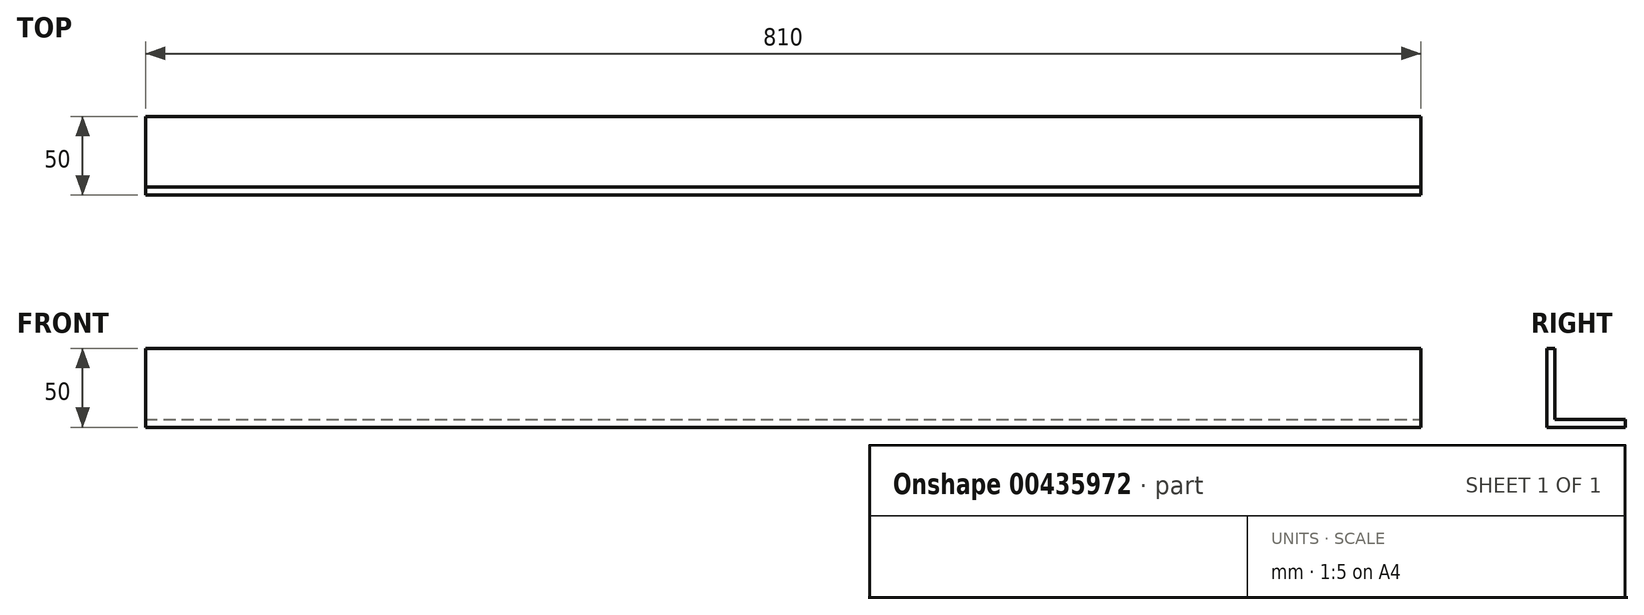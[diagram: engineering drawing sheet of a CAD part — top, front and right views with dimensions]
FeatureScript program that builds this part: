
annotation { "Feature Type Name" : "Feature", "Feature Type Description" : "" }
export const myFeature = defineFeature(function(context is Context, id is Id, definition is map)
    precondition{}
    {
        {
            var Q0;
            Q0=qCreatedBy(makeId("Right.planeOp"),FACE);
            var sketch = newSketch(context, id + "F0", { "sketchPlane" : qUnion([Q0])});
            skLineSegment(sketch, "E0.bottom", {"start": v(0, 0) * mm, "end": v(-50, 0) * mm});
            skLineSegment(sketch, "E0.right", {"start": v(-50, 0) * mm, "end": v(-50, 50) * mm});
            skLineSegment(sketch, "E1.0", {"start": v(0, 5) * mm, "end": v(-45, 5) * mm});
            skLineSegment(sketch, "E2.0", {"start": v(-45, 5) * mm, "end": v(-45, 50) * mm});
            skLineSegment(sketch, "E3", {"start": v(-50, 50) * mm, "end": v(-45, 50) * mm});
            skLineSegment(sketch, "E4", {"start": v(0, 5) * mm, "end": v(0, 0) * mm});
            skSolve(sketch);
        }
        {
            var Q0;
            Q0 = qSketchRegion(id + "F0", true);
            extrude(context, id + "F1", {"entities" : qUnion([Q0]), "oppositeDirection" : true, "depth" : 810 * mm});
        }
    });
